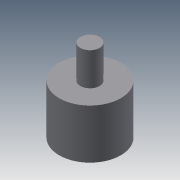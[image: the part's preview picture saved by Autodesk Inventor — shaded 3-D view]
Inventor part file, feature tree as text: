
AUTODESK INVENTOR PART (.ipt)
format: ipt  version: 2015 (Build 190159000, 159)  size: 89,600 bytes
history: native  units: mm
features: sketch x3, extrude x2, plane x1, hole x1
ambient origin geometry x8: Origin, YZ Plane, XZ Plane, XY Plane, X Axis, Y Axis, Z Axis, Center Point
bodies: Solid1 (feature_tree)
feature tree (7):
  extrude  "Extrusion1"  Depth=9.0mm TaperAngle=0.0deg
  plane  "Work Plane1"
  hole  "Hole1"  [1 undecoded]
  extrude  "Extrusion3"  Depth=6.0mm TaperAngle=0.0deg
  sketch  "Sketch1"  dims[d0=11.2mm d1=9.0mm d2=0.0mm]
  sketch  "Sketch3"  dims[d9=2.4mm]
  sketch  "Sketch4"  dims[d10=2.459mm d11=5.6mm d12=4.0mm d13=2.0mm d14=90.0deg d15=5.6mm d16=0.0mm d17=3.5mm d18=6.0mm d19=0.0mm]
note: 1 required parameter value undecoded (feature->parameter linkage not recoverable at this tier; creation-order binding heuristic only, values carry confidence <= 0.55)
